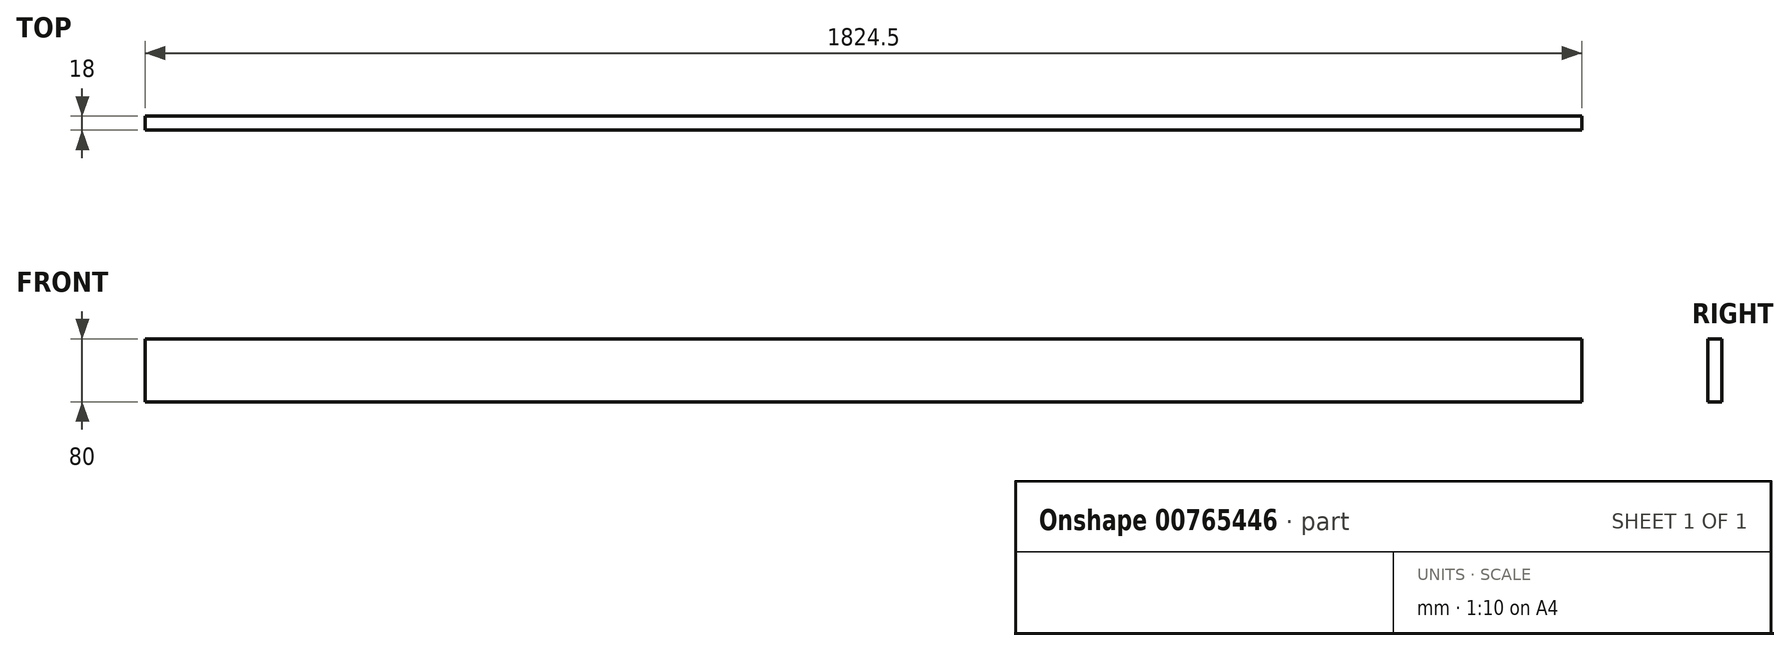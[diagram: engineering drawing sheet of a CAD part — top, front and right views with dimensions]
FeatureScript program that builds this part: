
annotation { "Feature Type Name" : "Feature", "Feature Type Description" : "" }
export const myFeature = defineFeature(function(context is Context, id is Id, definition is map)
    precondition{}
    {
        {
            var Q0;
            Q0=qCreatedBy(makeId("Front.planeOp"),FACE);
            var sketch = newSketch(context, id + "F0", { "sketchPlane" : qUnion([Q0])});
            skLineSegment(sketch, "E0.bottom", {"start": v(-912.25, -40) * mm, "end": v(912.25, -40) * mm});
            skLineSegment(sketch, "E0.top", {"start": v(-912.25, 40) * mm, "end": v(912.25, 40) * mm});
            skLineSegment(sketch, "E0.left", {"start": v(-912.25, -40) * mm, "end": v(-912.25, 40) * mm});
            skLineSegment(sketch, "E0.right", {"start": v(912.25, -40) * mm, "end": v(912.25, 40) * mm});
            skPoint(sketch, "E0.middle", {"position": v(0, 0) * mm});
            skSolve(sketch);
        }
        {
            var Q0;
            Q0 = qSketchRegion(id + "F0", true);
            extrude(context, id + "F1", {"entities" : qUnion([Q0]), "depth" : 18 * mm, "offsetDistance" : 25 * mm});
        }
    });
